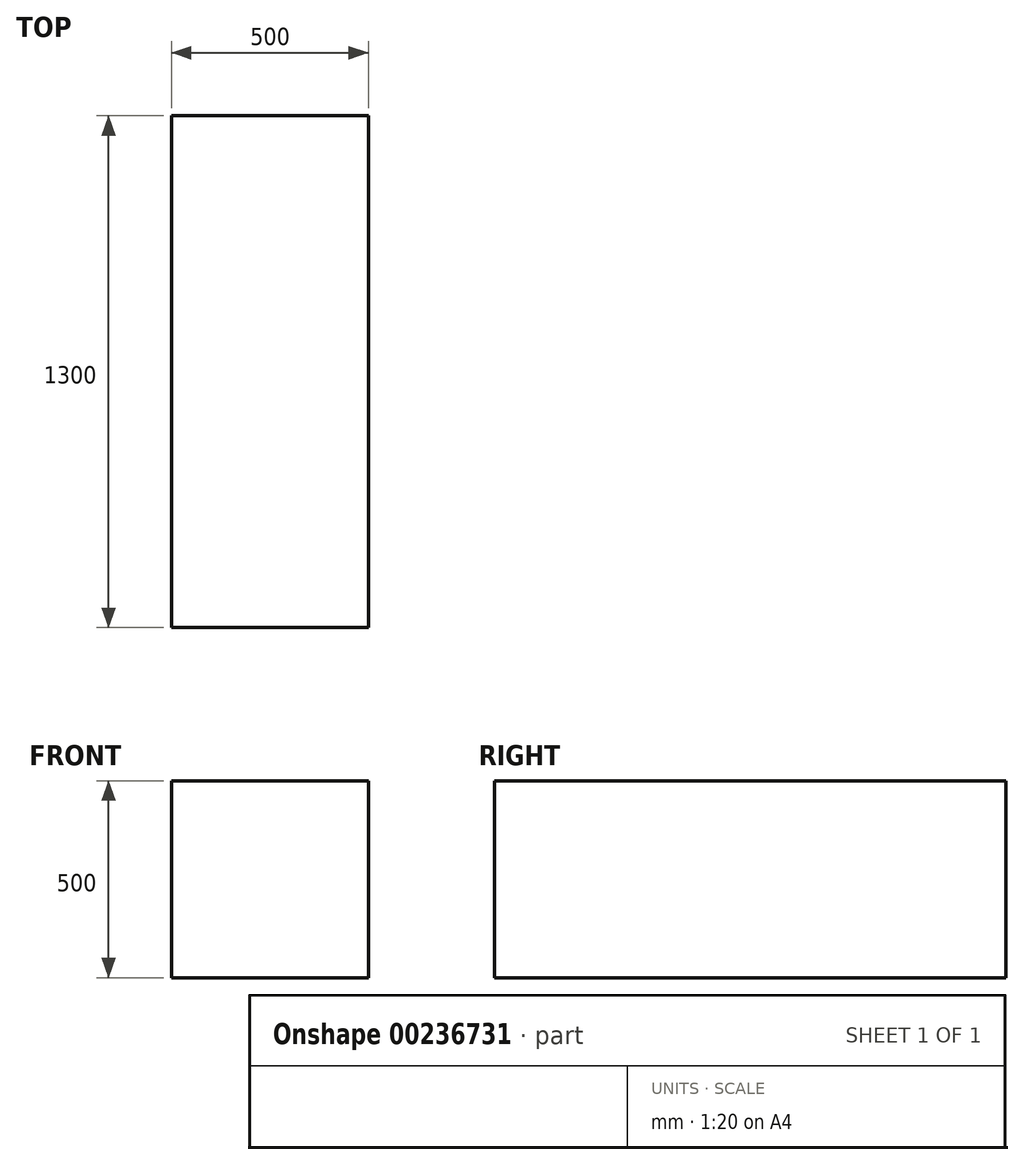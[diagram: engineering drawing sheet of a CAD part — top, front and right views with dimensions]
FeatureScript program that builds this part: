
annotation { "Feature Type Name" : "Feature", "Feature Type Description" : "" }
export const myFeature = defineFeature(function(context is Context, id is Id, definition is map)
    precondition{}
    {
        {
            var Q0;
            Q0=qCreatedBy(makeId("Front.planeOp"), FACE);
            var sketch = newSketch(context, id + "F0", { "sketchPlane" : qUnion([Q0])});
            skLineSegment(sketch, "E0.bottom", {"start": v(0, 0) * mm, "end": v(500, 0) * mm});
            skLineSegment(sketch, "E0.top", {"start": v(0, 500) * mm, "end": v(500, 500) * mm});
            skLineSegment(sketch, "E0.left", {"start": v(0, 0) * mm, "end": v(0, 500) * mm});
            skLineSegment(sketch, "E0.right", {"start": v(500, 0) * mm, "end": v(500, 500) * mm});
            skSolve(sketch);
        }
        {
            var Q0;
            Q0 = qSketchRegion(id + "F0", true);
            extrude(context, id + "F1", {"entities" : qUnion([Q0]), "depth" : 1300 * mm, "offsetDistance" : 25 * mm});
        }
    });
